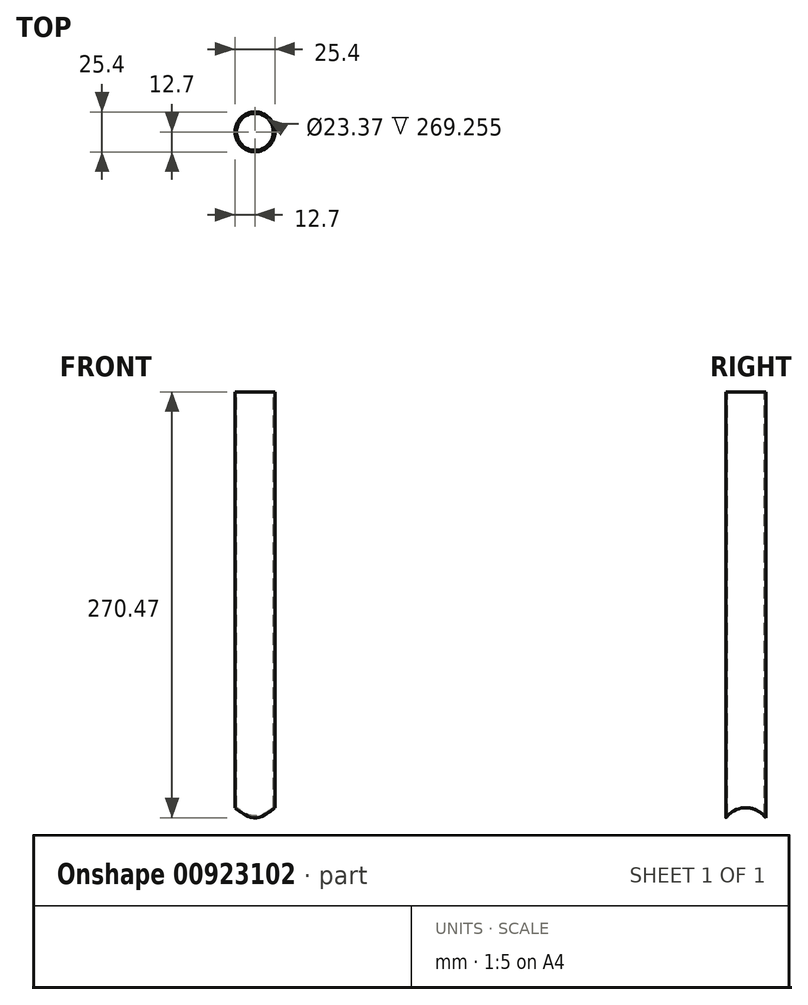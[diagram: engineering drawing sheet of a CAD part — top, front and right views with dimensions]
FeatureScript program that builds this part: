
annotation { "Feature Type Name" : "Feature", "Feature Type Description" : "" }
export const myFeature = defineFeature(function(context is Context, id is Id, definition is map)
    precondition{}
    {
        {
            var Q0;
            Q0=qCreatedBy(makeId("Top.planeOp"),FACE);
            var sketch = newSketch(context, id + "F0", { "sketchPlane" : qUnion([Q0])});
            skCircle(sketch, "E0", {"center": v(0, 0) * mm, "radius": 12.7 * mm});
            skSolve(sketch);
        }
        {
            var Q0;
            Q0=makeQuery(id+"F0.imprint","IMPRINT",FACE,{"disambiguationData":[TD([[makeQuery(id+"F0.imprint","IMPRINT",EDGE,{"derivedFrom":sQuery(id+"F0.wireOp",EDGE,"E0")}),1.0]])]});
            extrude(context, id + "F1", {"entities" : qUnion([Q0]), "depth" : 280 * mm, "offsetDistance" : 25 * mm});
        }
        {
            var Q0;
            Q0=qCreatedBy(makeId("Right.planeOp"),FACE);
            var sketch = newSketch(context, id + "F2", { "sketchPlane" : qUnion([Q0])});
            skCircle(sketch, "E1", {"center": v(0, 0) * mm, "radius": 15.88 * mm});
            skSolve(sketch);
        }
        {
            var Q0;
            Q0 = qSketchRegion(id + "F2", true);
            extrude(context, id + "F3", {"entities" : qUnion([Q0]), "operationType" : NewBodyOperationType.REMOVE, "endBound" : BoundingType.SYMMETRIC, "oppositeDirection" : true, "depth" : 100 * mm, "offsetDistance" : 25 * mm});
        }
        {
            var Q0;
            Q0=makeQuery(id+"F1.opExtrude","CAP_FACE",FACE,{"disambiguationData":[OSD([sQuery(id+"F0.wireOp",EDGE,"E0")])],"isStart":false});
            var sketch = newSketch(context, id + "F4", { "sketchPlane" : qUnion([Q0])});
            skCircle(sketch, "E2", {"center": v(0, 0) * mm, "radius": 11.68 * mm});
            skLineSegment(sketch, "E3", {"start": v(11.68, 0) * mm, "end": v(12.7, 0) * mm, "construction": true});
            skSolve(sketch);
        }
        {
            var Q0;
            Q0 = qSketchRegion(id + "F4", true);
            extrude(context, id + "F5", {"entities" : qUnion([Q0]), "operationType" : NewBodyOperationType.REMOVE, "endBound" : BoundingType.THROUGH_ALL, "oppositeDirection" : true, "depth" : 25 * mm, "offsetDistance" : 25 * mm});
        }
    });
